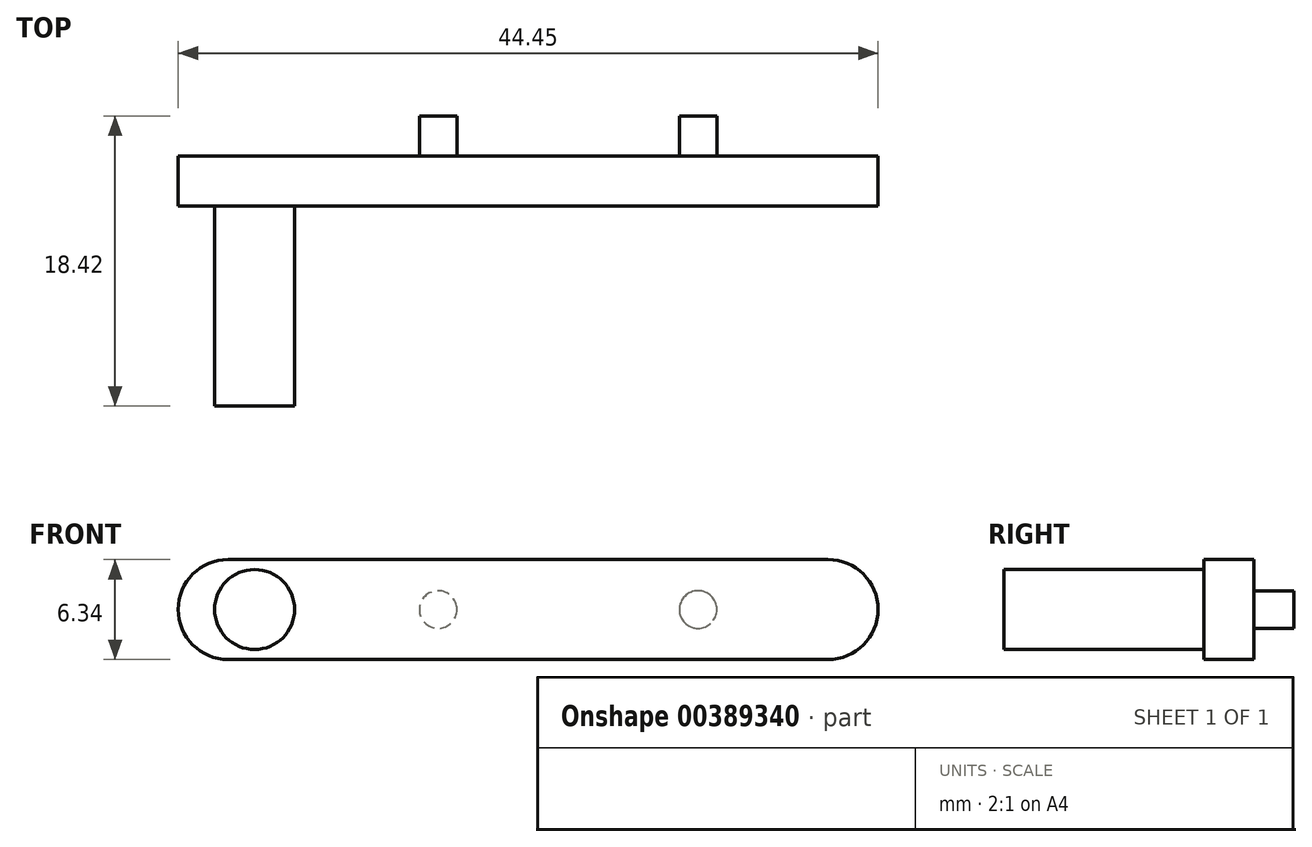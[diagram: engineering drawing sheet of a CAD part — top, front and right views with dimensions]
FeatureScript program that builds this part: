
annotation { "Feature Type Name" : "Feature", "Feature Type Description" : "" }
export const myFeature = defineFeature(function(context is Context, id is Id, definition is map)
    precondition{}
    {
        {
            var Q0;
            Q0=qCreatedBy(makeId("Front.planeOp"),FACE);
            var sketch = newSketch(context, id + "F0", { "sketchPlane" : qUnion([Q0])});
            skArc(sketch, "E0", {"start": v(3.18, 3.17) * mm, "mid": v(0, 0) * mm, "end": v(3.18, -3.18) * mm});
            skArc(sketch, "E1", {"start": v(41.27, -3.18) * mm, "mid": v(44.45, 0) * mm, "end": v(41.27, 3.17) * mm});
            skLineSegment(sketch, "E2", {"start": v(3.18, 3.18) * mm, "end": v(41.27, 3.18) * mm});
            skLineSegment(sketch, "E3", {"start": v(3.18, -3.18) * mm, "end": v(41.27, -3.18) * mm});
            skSolve(sketch);
        }
        {
            var Q0;
            Q0=makeQuery(id+"F0.imprint","IMPRINT",FACE,{"disambiguationData":[TD([[makeQuery(id+"F0.imprint","IMPRINT",EDGE,{"derivedFrom":sQuery(id+"F0.wireOp",EDGE,"E0")}),1.0]])]});
            extrude(context, id + "F1", {"entities" : qUnion([Q0]), "depth" : 3.17 * mm});
        }
        {
            var Q0;
            Q0=makeQuery(id+"F1.opExtrude","CAP_FACE",FACE,{"disambiguationData":[OSD([sQuery(id+"F0.wireOp",EDGE,"E0"),sQuery(id+"F0.wireOp",EDGE,"E1"),sQuery(id+"F0.wireOp",EDGE,"E2"),sQuery(id+"F0.wireOp",EDGE,"E3")])],"isStart":false});
            var sketch = newSketch(context, id + "F2", { "sketchPlane" : qUnion([Q0])});
            skCircle(sketch, "E4", {"center": v(4.85, 0) * mm, "radius": 2.54 * mm});
            skPoint(sketch, "E4.centerSnap0", {"position": v(0, 0) * mm});
            skSolve(sketch);
        }
        {
            var Q0;
            Q0 = qSketchRegion(id + "F2", true);
            extrude(context, id + "F3", {"entities" : qUnion([Q0]), "operationType" : NewBodyOperationType.ADD, "depth" : 12.7 * mm});
        }
        {
            var Q0;
            Q0=makeQuery(id+"F1.opExtrude","CAP_FACE",FACE,{"disambiguationData":[OSD([sQuery(id+"F0.wireOp",EDGE,"E0"),sQuery(id+"F0.wireOp",EDGE,"E1"),sQuery(id+"F0.wireOp",EDGE,"E2"),sQuery(id+"F0.wireOp",EDGE,"E3")])],"isStart":true});
            var sketch = newSketch(context, id + "F4", { "sketchPlane" : qUnion([Q0])});
            skCircle(sketch, "E5", {"center": v(-16.51, 0) * mm, "radius": 1.2 * mm});
            skCircle(sketch, "E6", {"center": v(-33.02, 0) * mm, "radius": 1.2 * mm});
            skSolve(sketch);
        }
        {
            var Q0;
            Q0 = qSketchRegion(id + "F4", true);
            extrude(context, id + "F5", {"entities" : qUnion([Q0]), "operationType" : NewBodyOperationType.ADD, "depth" : 2.54 * mm});
        }
    });
